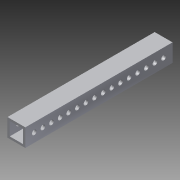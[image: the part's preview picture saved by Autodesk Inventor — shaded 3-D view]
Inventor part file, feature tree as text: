
AUTODESK INVENTOR PART (.ipt)
format: ipt  version: 2013 (Build 170138000, 138)  size: 130,560 bytes
history: native  units: in
note: dims shown in document units (in); Inventor stores cm internally (conversion verified against a paired STEP export)
features: extrude x2, sketch x1
ambient origin geometry x8: Origin, YZ Plane, XZ Plane, XY Plane, X Axis, Y Axis, Z Axis, Center Point
bodies: Solid1 (feature_tree)
feature tree (3):
  extrude  "Extrusion1"  Depth=1.0in
  extrude  "Extrusion2"  Depth=0.125in
  sketch  "Sketch1"  dims[d0=1.0in d1=1.0in d2=0.125in d3=8.25in d4=0.0in d5=0.5in d7=0.26in d8=16.5in d9=0.0in d13=8.25in d14=6.2992in d16=0.4833in d17=0.3937in d19=1.0in]
